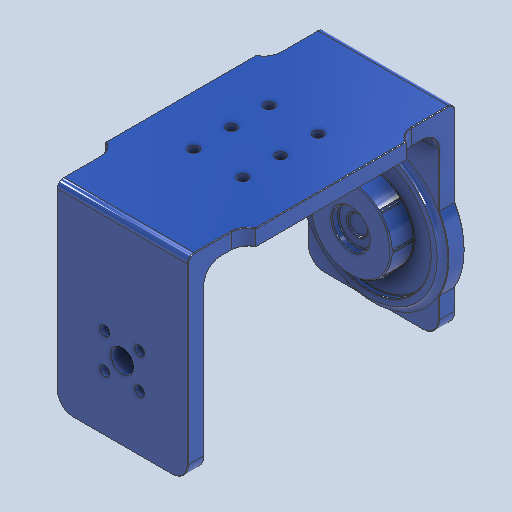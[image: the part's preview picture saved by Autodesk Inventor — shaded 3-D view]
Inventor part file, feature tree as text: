
AUTODESK INVENTOR PART (.ipt)
format: ipt  version: 2022 (Build 260153000, 153)  size: 744,448 bytes
history: native  units: mm
features: extrude x12, sketch x12, fillet x9, other x6, projected_geometry x2, mirror x1, pattern_circular x1, chamfer x1, revolve x1
ambient origin geometry x8: Origin, YZ Plane, XZ Plane, XY Plane, X Axis, Y Axis, Z Axis, Center Point
bodies: Body1 (feature_tree)
feature tree (45):
  other  "Твердое тело1"
  extrude  "Выдавливание1"  Depth=40.0mm
  extrude  "Выдавливание5"  Depth=81.5mm
  fillet  "Сопряжение3"  Radius=5.0mm
  other  "РабПлоскость1"
  extrude  "Выдавливание6"  Depth=45.8mm
  fillet  "Сопряжение4"  Radius=25.0mm
  fillet  "Сопряжение5"  Radius=3.0mm
  mirror  "Зеркальное отражение2"
  extrude  "Выдавливание7"  Depth=5.0mm
  other  "РабОсь6"
  extrude  "Выдавливание8"  Depth=55.0mm
  extrude  "Выдавливание9"  Depth=5.0mm TaperAngle=0.0deg
  extrude  "Выдавливание10"  Depth=5.0mm
  fillet  "Сопряжение7"  Radius=5.0mm
  other  "РабОсь1"
  pattern_circular  "Круговой массив1"  Count=4  [1 undecoded]
  fillet  "Сопряжение8"  Radius=7.0mm
  fillet  "Сопряжение11"  Radius=3.0mm
  other  "РабПлоскость3"
  extrude  "Выдавливание14"  Depth=37.8mm
  fillet  "Сопряжение13"  Radius=2.0mm
  fillet  "Сопряжение14"  Radius=1.4mm
  extrude  "Выдавливание16"  Depth=24.7mm
  extrude  "Выдавливание17"  Depth=6.9mm TaperAngle=0.0deg
  fillet  "Сопряжение16"  Radius=0.5mm
  extrude  "Выдавливание18"  Depth=1.4mm TaperAngle=0.0deg
  chamfer  "Фаска2"  Distance=0.4mm
  other  "РабПлоскость4"
  revolve  "Вращение1"
  extrude  "Выдавливание19"  Depth=80.0mm TaperAngle=360.0deg
  sketch  "Эскиз1"
  sketch  "Эскиз5"
  sketch  "Эскиз6"
  sketch  "Эскиз7"
  projected_geometry  "Спроецированная петля1"
  sketch  "Эскиз9"
  sketch  "Эскиз10"
  sketch  "Эскиз17"
  sketch  "Эскиз19"
  sketch  "Эскиз20"
  projected_geometry  "Спроецированная петля3"
  sketch  "Эскиз21"
  sketch  "Эскиз22"
  sketch  "Эскиз23"
note: 1 required parameter value undecoded (feature->parameter linkage not recoverable at this tier; creation-order binding heuristic only, values carry confidence <= 0.55)
